# Revit family: Kohler Loure 14602A-4ND-CP Family
name_source: partatom
category: Plumbing Fixtures
revit_build: Autodesk Revit 2018 (Build: 20181011_1500(x64)
units: mm (PartAtom-declared; Revit-internal decimal feet)

## family parameters
Always vertical = Yes
Cut with Voids When Loaded = No
Part Type = Normal
Room Calculation Point = No
Round Connector Dimension = Use Diameter
Shared = No
Work Plane-Based = No

## types (1)
- Kohler Loure 14602A-4ND-CP
    Disclaimer = Although care has been taken to ensure, to the best of our knowledge, that all data and information contained herein is accurate to the extent that it relates to either matters of fact or accepted practice at the time of issue. MDFC (Pty) Ltd assumes no responsibility for any errors in, or misinterpretation of, such data and/ or information or any loss or damage arising from, or related to its use
    Length = 202 mm
    Manufacturer = Kohler Co.
    Material = Chrome
    Model = Kohler Loure 14602A-4ND-CP
    Telephone = 011 050 9000
    URL = www.africa.kohler.com
    Width = 200 mm

## geometry (parser evidence)
native form markers: Sweep x3
no freeform markers — native parametric forms only
